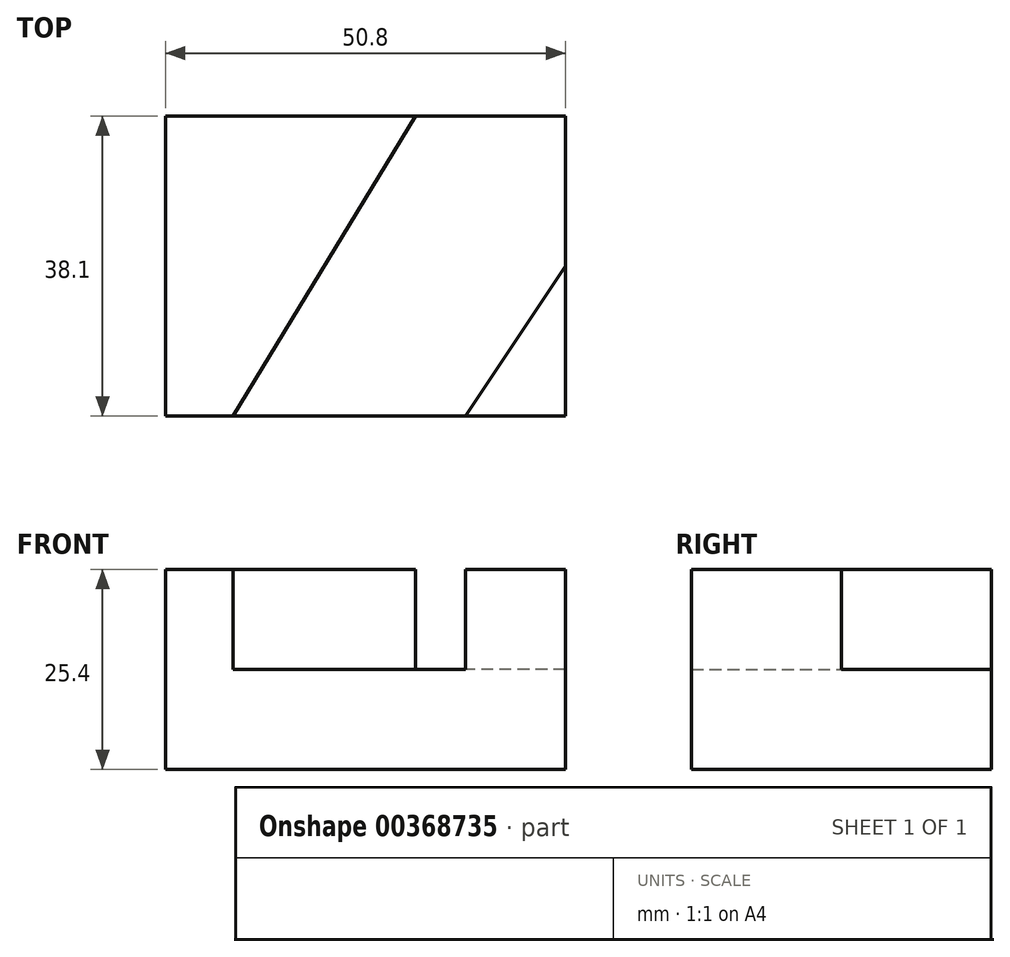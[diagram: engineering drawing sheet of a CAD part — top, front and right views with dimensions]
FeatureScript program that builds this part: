
annotation { "Feature Type Name" : "Feature", "Feature Type Description" : "" }
export const myFeature = defineFeature(function(context is Context, id is Id, definition is map)
    precondition{}
    {
        {
            var Q0;
            Q0=qCreatedBy(makeId("Top.planeOp"),FACE);
            var sketch = newSketch(context, id + "F0", { "sketchPlane" : qUnion([Q0])});
            skLineSegment(sketch, "E0", {"start": v(0, 0) * mm, "end": v(50.8, 0) * mm});
            skLineSegment(sketch, "E1", {"start": v(50.8, 0) * mm, "end": v(50.8, 38.1) * mm});
            skLineSegment(sketch, "E2", {"start": v(50.8, 38.1) * mm, "end": v(0, 38.1) * mm});
            skLineSegment(sketch, "E3", {"start": v(0, 38.1) * mm, "end": v(0, 0) * mm});
            skSolve(sketch);
        }
        {
            var Q0;
            Q0 = qSketchRegion(id + "F0", true);
            extrude(context, id + "F1", {"entities" : qUnion([Q0]), "depth" : 25.4 * mm});
        }
        {
            var Q0;
            Q0=makeQuery(id+"F1.opExtrude","CAP_FACE",FACE,{"disambiguationData":[OSD([sQuery(id+"F0.wireOp",EDGE,"E0"),sQuery(id+"F0.wireOp",EDGE,"E1"),sQuery(id+"F0.wireOp",EDGE,"E2"),sQuery(id+"F0.wireOp",EDGE,"E3")])],"isStart":false});
            var sketch = newSketch(context, id + "F2", { "sketchPlane" : qUnion([Q0])});
            skLineSegment(sketch, "E4", {"start": v(0, 0) * mm, "end": v(8.57, 0) * mm});
            skLineSegment(sketch, "E5", {"start": v(8.57, 0) * mm, "end": v(31.75, 38.1) * mm});
            skLineSegment(sketch, "E6", {"start": v(31.75, 38.1) * mm, "end": v(50.8, 38.1) * mm});
            skLineSegment(sketch, "E7", {"start": v(50.8, 38.1) * mm, "end": v(50.8, 19.05) * mm});
            skLineSegment(sketch, "E8", {"start": v(50.8, 19.05) * mm, "end": v(38.1, 0) * mm});
            skLineSegment(sketch, "E9", {"start": v(38.1, 0) * mm, "end": v(50.8, 0) * mm});
            skLineSegment(sketch, "E10", {"start": v(50.8, 0) * mm, "end": v(0, 0) * mm});
            skSolve(sketch);
        }
        {
            var Q0;
            {var subQ1=sQuery(id+"F2.wireOp",EDGE,"E5");Q0=makeQuery(id+"F2.imprint","IMPRINT",FACE,{"disambiguationData":[TD([[makeQuery(id+"F2.imprint","IMPRINT",EDGE,{"derivedFrom":subQ1}),-1.0]])]});}
            extrude(context, id + "F3", {"entities" : qUnion([Q0]), "operationType" : NewBodyOperationType.REMOVE, "oppositeDirection" : true, "depth" : 12.7 * mm});
        }
    });
